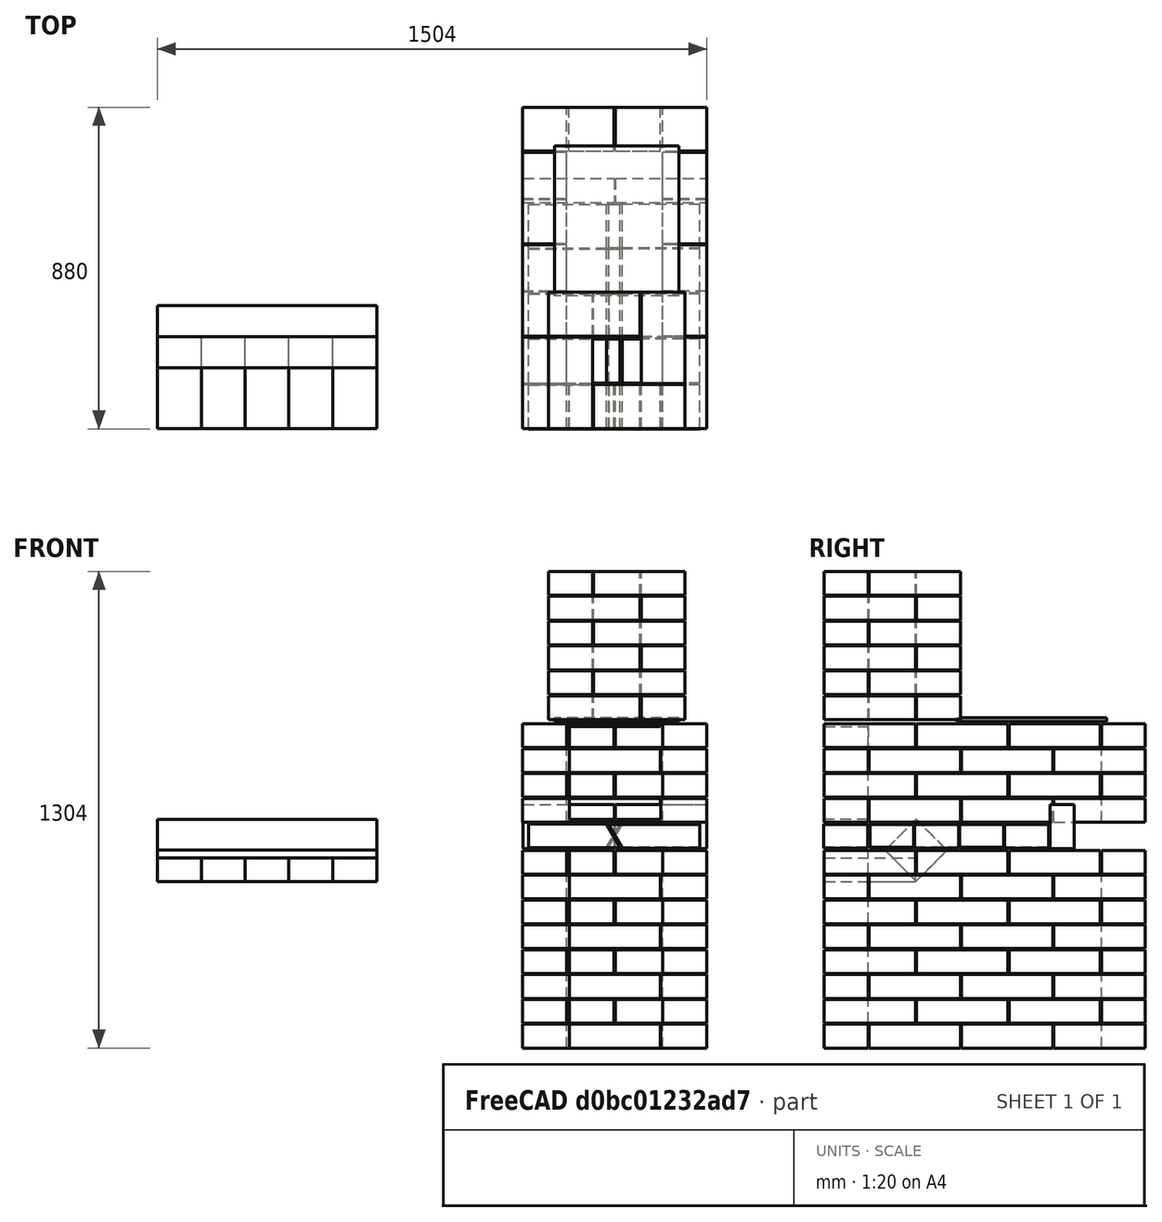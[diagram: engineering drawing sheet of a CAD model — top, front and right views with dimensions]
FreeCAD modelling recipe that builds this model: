
FCSTD DOCUMENT  (FreeCAD 0.19R24291 (Git))
Label: МиниАрийка
License: All rights reserved
LicenseURL: http://en.wikipedia.org/wiki/All_rights_reserved
objects: Part::Box×169, Part::Compound×30, Part::Cut×12, Part::Mirroring×2
note: 213 computed .brp shape members not serialized (recipe doc carries the construction recipe); baked Part::Feature solids carry a one-line shape summary decoded from their .brp

FEATURE [Part::Box] Box1  label="Куб1"
  AttacherType = Attacher::AttachEngine3D
  Height = 65
  Length = 250
  Width = 120
FEATURE [Part::Box] Box2  label="Куб2"
  AttacherType = Attacher::AttachEngine3D
  Height = 65
  Length = 250
  Placement = pos=(253,0,0) rot=(0,0,1;0rad)
  Width = 120
FEATURE [Part::Box] Box3  label="Куб3"
  AttacherType = Attacher::AttachEngine3D
  Height = 65
  Length = 250
  Placement = pos=(126.5,759,0) rot=(0,0,1;0rad)
  Width = 120
FEATURE [Part::Box] Box4  label="Куб4"
  AttacherType = Attacher::AttachEngine3D
  Height = 65
  Length = 250
  Placement = pos=(120,123,0) rot=(0,0,1;1.5708rad)
  Width = 120
FEATURE [Part::Box] Box5  label="Куб5"
  AttacherType = Attacher::AttachEngine3D
  Height = 65
  Length = 250
  Placement = pos=(120,376,0) rot=(0,0,1;1.5708rad)
  Width = 120
FEATURE [Part::Box] Box6  label="Куб6"
  AttacherType = Attacher::AttachEngine3D
  Height = 65
  Length = 250
  Placement = pos=(120,629,0) rot=(0,0,1;1.5708rad)
  Width = 120
FEATURE [Part::Box] Box7  label="Куб7"
  AttacherType = Attacher::AttachEngine3D
  Height = 65
  Length = 250
  Placement = pos=(503,123,0) rot=(0,0,1;1.5708rad)
  Width = 120
FEATURE [Part::Box] Box8  label="Куб8"
  AttacherType = Attacher::AttachEngine3D
  Height = 65
  Length = 250
  Placement = pos=(503,376,0) rot=(0,0,1;1.5708rad)
  Width = 120
FEATURE [Part::Box] Box9  label="Куб9"
  AttacherType = Attacher::AttachEngine3D
  Height = 65
  Length = 250
  Placement = pos=(503,629,0) rot=(0,0,1;1.5708rad)
  Width = 120
FEATURE [Part::Compound] Compound_row0
  Links = -> [Box1,Box2,Box3,Box4,Box5,Box6,Box7,Box8,Box9]
FEATURE [Part::Box] Box10  label="Куб10"
  AttacherType = Attacher::AttachEngine3D
  Height = 65
  Length = 250
  Placement = pos=(0,759,68) rot=(0,0,1;0rad)
  Width = 120
FEATURE [Part::Box] Box11  label="Куб11"
  AttacherType = Attacher::AttachEngine3D
  Height = 65
  Length = 250
  Placement = pos=(253,759,68) rot=(0,0,1;0rad)
  Width = 120
FEATURE [Part::Box] Box12  label="Куб12"
  AttacherType = Attacher::AttachEngine3D
  Height = 65
  Length = 250
  Placement = pos=(126.5,0,68) rot=(0,0,1;0rad)
  Width = 120
FEATURE [Part::Box] Box13  label="Куб13"
  AttacherType = Attacher::AttachEngine3D
  Height = 65
  Length = 250
  Placement = pos=(120,0,68) rot=(0,0,1;1.5708rad)
  Width = 120
FEATURE [Part::Box] Box14  label="Куб14"
  AttacherType = Attacher::AttachEngine3D
  Height = 65
  Length = 250
  Placement = pos=(120,253,68) rot=(0,0,1;1.5708rad)
  Width = 120
FEATURE [Part::Box] Box15  label="Куб15"
  AttacherType = Attacher::AttachEngine3D
  Height = 65
  Length = 250
  Placement = pos=(120,506,68) rot=(0,0,1;1.5708rad)
  Width = 120
FEATURE [Part::Box] Box16  label="Куб16"
  AttacherType = Attacher::AttachEngine3D
  Height = 65
  Length = 250
  Placement = pos=(503,0,68) rot=(0,0,1;1.5708rad)
  Width = 120
FEATURE [Part::Box] Box17  label="Куб17"
  AttacherType = Attacher::AttachEngine3D
  Height = 65
  Length = 250
  Placement = pos=(503,253,68) rot=(0,0,1;1.5708rad)
  Width = 120
FEATURE [Part::Box] Box18  label="Куб18"
  AttacherType = Attacher::AttachEngine3D
  Height = 65
  Length = 250
  Placement = pos=(503,506,68) rot=(0,0,1;1.5708rad)
  Width = 120
FEATURE [Part::Compound] Compound_row1
  Links = -> [Box10,Box11,Box12,Box13,Box14,Box15,Box16,Box17,Box18]
FEATURE [Part::Box] Box19  label="Куб19"
  AttacherType = Attacher::AttachEngine3D
  Height = 65
  Length = 250
  Placement = pos=(0,0,136) rot=(0,0,1;0rad)
  Width = 120
FEATURE [Part::Box] Box20  label="Куб20"
  AttacherType = Attacher::AttachEngine3D
  Height = 65
  Length = 250
  Placement = pos=(253,0,136) rot=(0,0,1;0rad)
  Width = 120
FEATURE [Part::Box] Box21  label="Куб21"
  AttacherType = Attacher::AttachEngine3D
  Height = 65
  Length = 250
  Placement = pos=(126.5,759,136) rot=(0,0,1;0rad)
  Width = 120
FEATURE [Part::Box] Box22  label="Куб22"
  AttacherType = Attacher::AttachEngine3D
  Height = 65
  Length = 250
  Placement = pos=(120,123,136) rot=(0,0,1;1.5708rad)
  Width = 120
FEATURE [Part::Box] Box23  label="Куб23"
  AttacherType = Attacher::AttachEngine3D
  Height = 65
  Length = 250
  Placement = pos=(120,376,136) rot=(0,0,1;1.5708rad)
  Width = 120
FEATURE [Part::Box] Box24  label="Куб24"
  AttacherType = Attacher::AttachEngine3D
  Height = 65
  Length = 250
  Placement = pos=(120,629,136) rot=(0,0,1;1.5708rad)
  Width = 120
FEATURE [Part::Box] Box25  label="Куб25"
  AttacherType = Attacher::AttachEngine3D
  Height = 65
  Length = 250
  Placement = pos=(503,123,136) rot=(0,0,1;1.5708rad)
  Width = 120
FEATURE [Part::Box] Box26  label="Куб26"
  AttacherType = Attacher::AttachEngine3D
  Height = 65
  Length = 250
  Placement = pos=(503,376,136) rot=(0,0,1;1.5708rad)
  Width = 120
FEATURE [Part::Box] Box27  label="Куб27"
  AttacherType = Attacher::AttachEngine3D
  Height = 65
  Length = 250
  Placement = pos=(503,629,136) rot=(0,0,1;1.5708rad)
  Width = 120
FEATURE [Part::Compound] Compound_row2
  Links = -> [Box19,Box20,Box21,Box22,Box23,Box24,Box25,Box26,Box27]
FEATURE [Part::Box] Box28  label="Куб28"
  AttacherType = Attacher::AttachEngine3D
  Height = 65
  Length = 250
  Placement = pos=(0,759,204) rot=(0,0,1;0rad)
  Width = 120
FEATURE [Part::Box] Box29  label="Куб29"
  AttacherType = Attacher::AttachEngine3D
  Height = 65
  Length = 250
  Placement = pos=(253,759,204) rot=(0,0,1;0rad)
  Width = 120
FEATURE [Part::Box] Box30  label="Куб30"
  AttacherType = Attacher::AttachEngine3D
  Height = 65
  Length = 250
  Placement = pos=(126.5,0,204) rot=(0,0,1;0rad)
  Width = 120
FEATURE [Part::Box] Box31  label="Куб31"
  AttacherType = Attacher::AttachEngine3D
  Height = 65
  Length = 250
  Placement = pos=(120,0,204) rot=(0,0,1;1.5708rad)
  Width = 120
FEATURE [Part::Box] Box32  label="Куб32"
  AttacherType = Attacher::AttachEngine3D
  Height = 65
  Length = 250
  Placement = pos=(120,253,204) rot=(0,0,1;1.5708rad)
  Width = 120
FEATURE [Part::Box] Box33  label="Куб33"
  AttacherType = Attacher::AttachEngine3D
  Height = 65
  Length = 250
  Placement = pos=(120,506,204) rot=(0,0,1;1.5708rad)
  Width = 120
FEATURE [Part::Box] Box34  label="Куб34"
  AttacherType = Attacher::AttachEngine3D
  Height = 65
  Length = 250
  Placement = pos=(503,0,204) rot=(0,0,1;1.5708rad)
  Width = 120
FEATURE [Part::Box] Box35  label="Куб35"
  AttacherType = Attacher::AttachEngine3D
  Height = 65
  Length = 250
  Placement = pos=(503,253,204) rot=(0,0,1;1.5708rad)
  Width = 120
FEATURE [Part::Box] Box36  label="Куб36"
  AttacherType = Attacher::AttachEngine3D
  Height = 65
  Length = 250
  Placement = pos=(503,506,204) rot=(0,0,1;1.5708rad)
  Width = 120
FEATURE [Part::Compound] Compound_row3
  Links = -> [Box28,Box29,Box30,Box31,Box32,Box33,Box34,Box35,Box36]
FEATURE [Part::Box] Box37  label="Куб37"
  AttacherType = Attacher::AttachEngine3D
  Height = 65
  Length = 250
  Placement = pos=(0,0,272) rot=(0,0,1;0rad)
  Width = 120
FEATURE [Part::Box] Box38  label="Куб38"
  AttacherType = Attacher::AttachEngine3D
  Height = 65
  Length = 250
  Placement = pos=(253,0,272) rot=(0,0,1;0rad)
  Width = 120
FEATURE [Part::Box] Box39  label="Куб39"
  AttacherType = Attacher::AttachEngine3D
  Height = 65
  Length = 250
  Placement = pos=(126.5,759,272) rot=(0,0,1;0rad)
  Width = 120
FEATURE [Part::Box] Box40  label="Куб40"
  AttacherType = Attacher::AttachEngine3D
  Height = 65
  Length = 250
  Placement = pos=(120,123,272) rot=(0,0,1;1.5708rad)
  Width = 120
FEATURE [Part::Box] Box41  label="Куб41"
  AttacherType = Attacher::AttachEngine3D
  Height = 65
  Length = 250
  Placement = pos=(120,376,272) rot=(0,0,1;1.5708rad)
  Width = 120
FEATURE [Part::Box] Box42  label="Куб42"
  AttacherType = Attacher::AttachEngine3D
  Height = 65
  Length = 250
  Placement = pos=(120,629,272) rot=(0,0,1;1.5708rad)
  Width = 120
FEATURE [Part::Box] Box43  label="Куб43"
  AttacherType = Attacher::AttachEngine3D
  Height = 65
  Length = 250
  Placement = pos=(503,123,272) rot=(0,0,1;1.5708rad)
  Width = 120
FEATURE [Part::Box] Box44  label="Куб44"
  AttacherType = Attacher::AttachEngine3D
  Height = 65
  Length = 250
  Placement = pos=(503,376,272) rot=(0,0,1;1.5708rad)
  Width = 120
FEATURE [Part::Box] Box45  label="Куб45"
  AttacherType = Attacher::AttachEngine3D
  Height = 65
  Length = 250
  Placement = pos=(503,629,272) rot=(0,0,1;1.5708rad)
  Width = 120
FEATURE [Part::Compound] Compound_row4
  Links = -> [Box37,Box38,Box39,Box40,Box41,Box42,Box43,Box44,Box45]
FEATURE [Part::Box] Box46  label="Куб46"
  AttacherType = Attacher::AttachEngine3D
  Height = 65
  Length = 250
  Placement = pos=(0,759,340) rot=(0,0,1;0rad)
  Width = 120
FEATURE [Part::Box] Box47  label="Куб47"
  AttacherType = Attacher::AttachEngine3D
  Height = 65
  Length = 250
  Placement = pos=(253,759,340) rot=(0,0,1;0rad)
  Width = 120
FEATURE [Part::Box] Box48  label="Куб48"
  AttacherType = Attacher::AttachEngine3D
  Height = 65
  Length = 250
  Placement = pos=(126.5,0,340) rot=(0,0,1;0rad)
  Width = 120
FEATURE [Part::Box] Box49  label="Куб49"
  AttacherType = Attacher::AttachEngine3D
  Height = 65
  Length = 250
  Placement = pos=(120,0,340) rot=(0,0,1;1.5708rad)
  Width = 120
FEATURE [Part::Box] Box50  label="Куб50"
  AttacherType = Attacher::AttachEngine3D
  Height = 65
  Length = 250
  Placement = pos=(120,253,340) rot=(0,0,1;1.5708rad)
  Width = 120
FEATURE [Part::Box] Box51  label="Куб51"
  AttacherType = Attacher::AttachEngine3D
  Height = 65
  Length = 250
  Placement = pos=(120,506,340) rot=(0,0,1;1.5708rad)
  Width = 120
FEATURE [Part::Box] Box52  label="Куб52"
  AttacherType = Attacher::AttachEngine3D
  Height = 65
  Length = 250
  Placement = pos=(503,0,340) rot=(0,0,1;1.5708rad)
  Width = 120
FEATURE [Part::Box] Box53  label="Куб53"
  AttacherType = Attacher::AttachEngine3D
  Height = 65
  Length = 250
  Placement = pos=(503,253,340) rot=(0,0,1;1.5708rad)
  Width = 120
FEATURE [Part::Box] Box54  label="Куб54"
  AttacherType = Attacher::AttachEngine3D
  Height = 65
  Length = 250
  Placement = pos=(503,506,340) rot=(0,0,1;1.5708rad)
  Width = 120
FEATURE [Part::Compound] Compound_row5
  Links = -> [Box46,Box47,Box48,Box49,Box50,Box51,Box52,Box53,Box54]
FEATURE [Part::Box] Box55  label="Куб55"
  AttacherType = Attacher::AttachEngine3D
  Height = 65
  Length = 250
  Placement = pos=(0,0,408) rot=(0,0,1;0rad)
  Width = 120
FEATURE [Part::Box] Box56  label="Куб56"
  AttacherType = Attacher::AttachEngine3D
  Height = 65
  Length = 250
  Placement = pos=(253,0,408) rot=(0,0,1;0rad)
  Width = 120
FEATURE [Part::Box] Box57  label="Куб57"
  AttacherType = Attacher::AttachEngine3D
  Height = 65
  Length = 250
  Placement = pos=(126.5,759,408) rot=(0,0,1;0rad)
  Width = 120
FEATURE [Part::Box] Box58  label="Куб58"
  AttacherType = Attacher::AttachEngine3D
  Height = 65
  Length = 250
  Placement = pos=(120,123,408) rot=(0,0,1;1.5708rad)
  Width = 120
FEATURE [Part::Box] Box59  label="Куб59"
  AttacherType = Attacher::AttachEngine3D
  Height = 65
  Length = 250
  Placement = pos=(120,376,408) rot=(0,0,1;1.5708rad)
  Width = 120
FEATURE [Part::Box] Box60  label="Куб60"
  AttacherType = Attacher::AttachEngine3D
  Height = 65
  Length = 250
  Placement = pos=(120,629,408) rot=(0,0,1;1.5708rad)
  Width = 120
FEATURE [Part::Box] Box61  label="Куб61"
  AttacherType = Attacher::AttachEngine3D
  Height = 65
  Length = 250
  Placement = pos=(503,123,408) rot=(0,0,1;1.5708rad)
  Width = 120
FEATURE [Part::Box] Box62  label="Куб62"
  AttacherType = Attacher::AttachEngine3D
  Height = 65
  Length = 250
  Placement = pos=(503,376,408) rot=(0,0,1;1.5708rad)
  Width = 120
FEATURE [Part::Box] Box63  label="Куб63"
  AttacherType = Attacher::AttachEngine3D
  Height = 65
  Length = 250
  Placement = pos=(503,629,408) rot=(0,0,1;1.5708rad)
  Width = 120
FEATURE [Part::Compound] Compound_row6
  Links = -> [Box55,Box56,Box57,Box58,Box59,Box60,Box61,Box62,Box63]
FEATURE [Part::Box] Box64  label="Куб64"
  AttacherType = Attacher::AttachEngine3D
  Height = 65
  Length = 250
  Placement = pos=(0,759,476) rot=(0,0,1;0rad)
  Width = 120
FEATURE [Part::Box] Box65  label="Куб65"
  AttacherType = Attacher::AttachEngine3D
  Height = 65
  Length = 250
  Placement = pos=(253,759,476) rot=(0,0,1;0rad)
  Width = 120
FEATURE [Part::Box] Box66  label="Куб66"
  AttacherType = Attacher::AttachEngine3D
  Height = 65
  Length = 250
  Placement = pos=(126.5,0,476) rot=(0,0,1;0rad)
  Width = 120
FEATURE [Part::Box] Box67  label="Куб67"
  AttacherType = Attacher::AttachEngine3D
  Height = 65
  Length = 250
  Placement = pos=(120,0,476) rot=(0,0,1;1.5708rad)
  Width = 120
FEATURE [Part::Box] Box68  label="Куб68"
  AttacherType = Attacher::AttachEngine3D
  Height = 65
  Length = 250
  Placement = pos=(120,253,476) rot=(0,0,1;1.5708rad)
  Width = 120
FEATURE [Part::Box] Box69  label="Куб69"
  AttacherType = Attacher::AttachEngine3D
  Height = 65
  Length = 250
  Placement = pos=(120,506,476) rot=(0,0,1;1.5708rad)
  Width = 120
FEATURE [Part::Box] Box70  label="Куб70"
  AttacherType = Attacher::AttachEngine3D
  Height = 65
  Length = 250
  Placement = pos=(503,0,476) rot=(0,0,1;1.5708rad)
  Width = 120
FEATURE [Part::Box] Box71  label="Куб71"
  AttacherType = Attacher::AttachEngine3D
  Height = 65
  Length = 250
  Placement = pos=(503,253,476) rot=(0,0,1;1.5708rad)
  Width = 120
FEATURE [Part::Box] Box72  label="Куб72"
  AttacherType = Attacher::AttachEngine3D
  Height = 65
  Length = 250
  Placement = pos=(503,506,476) rot=(0,0,1;1.5708rad)
  Width = 120
FEATURE [Part::Compound] Compound_row7
  Links = -> [Box64,Box65,Box66,Box67,Box68,Box69,Box70,Box71,Box72]
FEATURE [Part::Box] Box090  label="Куб024"
  AttacherType = Attacher::AttachEngine3D
  Height = 65
  Length = 250
  Placement = pos=(120,0,455) rot=(0,0,1;1.5708rad)
  Width = 120
FEATURE [Part::Box] Box103  label="Куб029"
  AttacherType = Attacher::AttachEngine3D
  Height = 65
  Length = 250
  Placement = pos=(240,0,455) rot=(0,0,1;1.5708rad)
  Width = 120
FEATURE [Part::Box] Box104  label="Куб030"
  AttacherType = Attacher::AttachEngine3D
  Height = 65
  Length = 250
  Placement = pos=(360,0,455) rot=(0,0,1;1.5708rad)
  Width = 120
FEATURE [Part::Box] Box105  label="Куб031"
  AttacherType = Attacher::AttachEngine3D
  Height = 65
  Length = 250
  Placement = pos=(480,0,455) rot=(0,0,1;1.5708rad)
  Width = 120
FEATURE [Part::Box] Box106  label="Куб032"
  AttacherType = Attacher::AttachEngine3D
  Height = 65
  Length = 250
  Placement = pos=(600,0,455) rot=(0,0,1;1.5708rad)
  Width = 120
FEATURE [Part::Box] Box134  label="Куб049"
  AttacherType = Attacher::AttachEngine3D
  Height = 65
  Length = 250
  Placement = pos=(360,0,455) rot=(0,0,1;1.5708rad)
  Width = 120
FEATURE [Part::Box] Box135  label="Куб050"
  AttacherType = Attacher::AttachEngine3D
  Height = 65
  Length = 250
  Placement = pos=(480,0,455) rot=(0,0,1;1.5708rad)
  Width = 120
FEATURE [Part::Box] Box136  label="Куб051"
  AttacherType = Attacher::AttachEngine3D
  Height = 65
  Length = 250
  Placement = pos=(240,0,455) rot=(0,0,1;1.5708rad)
  Width = 120
FEATURE [Part::Box] Box137  label="Куб052"
  AttacherType = Attacher::AttachEngine3D
  Height = 65
  Length = 250
  Placement = pos=(600,0,455) rot=(0,0,1;1.5708rad)
  Width = 120
FEATURE [Part::Box] Box138  label="Куб053"
  AttacherType = Attacher::AttachEngine3D
  Height = 65
  Length = 250
  Placement = pos=(120,0,455) rot=(0,0,1;1.5708rad)
  Width = 120
FEATURE [Part::Compound] Compound039
  Links = -> [Box138,Box136,Box134,Box135,Box137]
  Placement = pos=(-1000,0,0) rot=(0,0,1;0rad)
FEATURE [Part::Box] Box139  label="Куб054"
  AttacherType = Attacher::AttachEngine3D
  Height = 120
  Length = 600
  Placement = pos=(-1000,251.73,456.377) rot=(1,0,0;0.785398rad)
  Width = 120
FEATURE [Part::Box] Box140  label="Куб055"
  AttacherType = Attacher::AttachEngine3D
  Height = 65
  Length = 250
  Placement = pos=(500,678,549) rot=(1,0,0;1.5708rad)
  Width = 120
FEATURE [Part::Box] Box141  label="Куб056"
  AttacherType = Attacher::AttachEngine3D
  Height = 65
  Length = 250
  Placement = pos=(753,678,549) rot=(1,0,0;1.5708rad)
  Width = 120
FEATURE [Part::Compound] Compound
  Links = -> [Box141,Box140]
  Placement = pos=(-499,6,-3) rot=(0,0,1;0rad)
FEATURE [Part::Box] Box  label="Топка"
  AttacherType = Attacher::AttachEngine3D
  Height = 545
  Length = 250
  Placement = pos=(128,-38,0) rot=(0,0,1;0rad)
  Width = 250
FEATURE [Part::Compound] Compound040
  Links = -> [Compound_row0,Compound_row1,Compound_row2,Compound_row3,Compound_row4,Compound_row5,Compound_row6,Compound_row7]
FEATURE [Part::Cut] Cut
  Base = -> Compound040
  Tool = -> Box
FEATURE [Part::Box] Box001  label="Куб001"
  AttacherType = Attacher::AttachEngine3D
  Height = 65
  Length = 250
  Placement = pos=(187.928,0,108.5) rot=(0,1,0;1.0472rad)
  Width = 120
FEATURE [Part::Box] Box142  label="Куб"
  AttacherType = Attacher::AttachEngine3D
  Height = 65
  Length = 250
  Width = 120
FEATURE [Part::Box] Box006  label="Куб006"
  AttacherType = Attacher::AttachEngine3D
  Height = 65
  Length = 250
  Placement = pos=(187.928,0,108.5) rot=(0,1,0;1.0472rad)
  Width = 120
FEATURE [Part::Box] Box007  label="Куб007"
  AttacherType = Attacher::AttachEngine3D
  Height = 65
  Length = 250
  Width = 120
FEATURE [Part::Cut] Cut003
  Base = -> Box007
  Placement = pos=(469,0,64) rot=(0,1,0;3.14159rad)
  Tool = -> Box006
FEATURE [Part::Box] Box005  label="Куб005"
  AttacherType = Attacher::AttachEngine3D
  Height = 65
  Length = 250
  Width = 120
FEATURE [Part::Box] Box008  label="Куб008"
  AttacherType = Attacher::AttachEngine3D
  Height = 65
  Length = 250
  Placement = pos=(187.928,0,108.5) rot=(0,1,0;1.0472rad)
  Width = 120
FEATURE [Part::Box] Box009  label="Куб009"
  AttacherType = Attacher::AttachEngine3D
  Height = 65
  Length = 250
  Width = 120
FEATURE [Part::Cut] Cut004
  Base = -> Box142
  Tool = -> Box001
FEATURE [Part::Box] Box002  label="Куб002"
  AttacherType = Attacher::AttachEngine3D
  Height = 65
  Length = 250
  Placement = pos=(187.928,0,108.5) rot=(0,1,0;1.0472rad)
  Width = 120
FEATURE [Part::Box] Box004  label="Куб004"
  AttacherType = Attacher::AttachEngine3D
  Height = 65
  Length = 250
  Placement = pos=(187.928,0,108.5) rot=(0,1,0;1.0472rad)
  Width = 120
FEATURE [Part::Cut] Cut002
  Base = -> Box005
  Tool = -> Box004
FEATURE [Part::Compound] Compound001
  Links = -> [Cut003,Cut002]
  Placement = pos=(0,123,0) rot=(0,0,1;0rad)
FEATURE [Part::Box] Box003  label="Куб003"
  AttacherType = Attacher::AttachEngine3D
  Height = 65
  Length = 250
  Width = 120
FEATURE [Part::Cut] Cut001
  Base = -> Box003
  Placement = pos=(469,0,64) rot=(0,1,0;3.14159rad)
  Tool = -> Box002
FEATURE [Part::Compound] Compound041
  Links = -> [Cut001,Cut004]
FEATURE [Part::Mirroring] Part__Mirroring  label="Compound (Mirror #1)"
  Base = (234.5,60,0)
  Normal = (0,0,1)
  Placement = pos=(0,0,65) rot=(0,0,1;0rad)
  Source = -> Compound041
FEATURE [Part::Box] Box012  label="Куб012"
  AttacherType = Attacher::AttachEngine3D
  Height = 65
  Length = 250
  Placement = pos=(187.928,0,108.5) rot=(0,1,0;1.0472rad)
  Width = 120
FEATURE [Part::Box] Box013  label="Куб013"
  AttacherType = Attacher::AttachEngine3D
  Height = 65
  Length = 250
  Width = 120
FEATURE [Part::Box] Box010  label="Куб010"
  AttacherType = Attacher::AttachEngine3D
  Height = 65
  Length = 250
  Width = 120
FEATURE [Part::Box] Box011  label="Куб011"
  AttacherType = Attacher::AttachEngine3D
  Height = 65
  Length = 250
  Placement = pos=(187.928,0,108.5) rot=(0,1,0;1.0472rad)
  Width = 120
FEATURE [Part::Cut] Cut005
  Base = -> Box010
  Tool = -> Box011
FEATURE [Part::Cut] Cut006
  Base = -> Box009
  Placement = pos=(469,0,64) rot=(0,1,0;3.14159rad)
  Tool = -> Box008
FEATURE [Part::Compound] Compound002
  Links = -> [Cut006,Cut005]
  Placement = pos=(0,246,0) rot=(0,0,1;0rad)
FEATURE [Part::Mirroring] Part__Mirroring001  label="Compound002 (Mirror #2)"
  Base = (0,0,0)
  Normal = (0,0,1)
  Placement = pos=(0,0,66) rot=(0,0,1;0rad)
  Source = -> Compound002
FEATURE [Part::Box] Box014  label="Куб014"
  AttacherType = Attacher::AttachEngine3D
  Height = 65
  Length = 250
  Width = 120
FEATURE [Part::Box] Box015  label="Куб015"
  AttacherType = Attacher::AttachEngine3D
  Height = 65
  Length = 250
  Placement = pos=(187.928,0,108.5) rot=(0,1,0;1.0472rad)
  Width = 120
FEATURE [Part::Cut] Cut007
  Base = -> Box014
  Tool = -> Box015
FEATURE [Part::Cut] Cut008
  Base = -> Box013
  Placement = pos=(469,0,64) rot=(0,1,0;3.14159rad)
  Tool = -> Box012
FEATURE [Part::Compound] Compound003
  Links = -> [Cut008,Cut007]
  Placement = pos=(0,369,0) rot=(0,0,1;0rad)
FEATURE [Part::Box] Box016  label="Куб016"
  AttacherType = Attacher::AttachEngine3D
  Height = 65
  Length = 250
  Placement = pos=(187.928,0,108.5) rot=(0,1,0;1.0472rad)
  Width = 120
FEATURE [Part::Box] Box017  label="Куб017"
  AttacherType = Attacher::AttachEngine3D
  Height = 65
  Length = 250
  Width = 120
FEATURE [Part::Cut] Cut009
  Base = -> Box017
  Placement = pos=(469,0,64) rot=(0,1,0;3.14159rad)
  Tool = -> Box016
FEATURE [Part::Box] Box018  label="Куб018"
  AttacherType = Attacher::AttachEngine3D
  Height = 65
  Length = 250
  Width = 120
FEATURE [Part::Box] Box019  label="Куб019"
  AttacherType = Attacher::AttachEngine3D
  Height = 65
  Length = 250
  Placement = pos=(187.928,0,108.5) rot=(0,1,0;1.0472rad)
  Width = 120
FEATURE [Part::Cut] Cut010
  Base = -> Box018
  Tool = -> Box019
FEATURE [Part::Compound] Compound004
  Links = -> [Cut009,Cut010]
  Placement = pos=(0,-126,0) rot=(0,0,1;0rad)
FEATURE [Part::Compound] Compound005
  Links = -> [Compound001,Compound003,Part__Mirroring,Part__Mirroring001,Compound004,Compound041,Compound002]
  Placement = pos=(16,125,548) rot=(0,0,1;0rad)
FEATURE [Part::Box] Box1043  label="Куб057"
  AttacherType = Attacher::AttachEngine3D
  Height = 65
  Length = 250
  Width = 120
FEATURE [Part::Box] Box2010  label="Куб058"
  AttacherType = Attacher::AttachEngine3D
  Height = 65
  Length = 250
  Placement = pos=(253,0,0) rot=(0,0,1;0rad)
  Width = 120
FEATURE [Part::Box] Box3010  label="Куб059"
  AttacherType = Attacher::AttachEngine3D
  Height = 65
  Length = 250
  Placement = pos=(126.5,759,0) rot=(0,0,1;0rad)
  Width = 120
FEATURE [Part::Box] Box4010  label="Куб060"
  AttacherType = Attacher::AttachEngine3D
  Height = 65
  Length = 250
  Placement = pos=(120,123,0) rot=(0,0,1;1.5708rad)
  Width = 120
FEATURE [Part::Box] Box5010  label="Куб061"
  AttacherType = Attacher::AttachEngine3D
  Height = 65
  Length = 250
  Placement = pos=(120,376,0) rot=(0,0,1;1.5708rad)
  Width = 120
FEATURE [Part::Box] Box6010  label="Куб062"
  AttacherType = Attacher::AttachEngine3D
  Height = 65
  Length = 250
  Placement = pos=(120,629,0) rot=(0,0,1;1.5708rad)
  Width = 120
FEATURE [Part::Box] Box7003  label="Куб063"
  AttacherType = Attacher::AttachEngine3D
  Height = 65
  Length = 250
  Placement = pos=(503,123,0) rot=(0,0,1;1.5708rad)
  Width = 120
FEATURE [Part::Box] Box8001  label="Куб064"
  AttacherType = Attacher::AttachEngine3D
  Height = 65
  Length = 250
  Placement = pos=(503,376,0) rot=(0,0,1;1.5708rad)
  Width = 120
FEATURE [Part::Box] Box9001  label="Куб065"
  AttacherType = Attacher::AttachEngine3D
  Height = 65
  Length = 250
  Placement = pos=(503,629,0) rot=(0,0,1;1.5708rad)
  Width = 120
FEATURE [Part::Compound] Compound_row0001
  Links = -> [Box1043,Box2010,Box3010,Box4010,Box5010,Box6010,Box7003,Box8001,Box9001]
FEATURE [Part::Box] Box10044  label="Куб066"
  AttacherType = Attacher::AttachEngine3D
  Height = 65
  Length = 250
  Placement = pos=(0,759,68) rot=(0,0,1;0rad)
  Width = 120
FEATURE [Part::Box] Box11001  label="Куб067"
  AttacherType = Attacher::AttachEngine3D
  Height = 65
  Length = 250
  Placement = pos=(253,759,68) rot=(0,0,1;0rad)
  Width = 120
FEATURE [Part::Box] Box12001  label="Куб068"
  AttacherType = Attacher::AttachEngine3D
  Height = 65
  Length = 250
  Placement = pos=(126.5,0,68) rot=(0,0,1;0rad)
  Width = 120
FEATURE [Part::Box] Box13010  label="Куб069"
  AttacherType = Attacher::AttachEngine3D
  Height = 65
  Length = 250
  Placement = pos=(120,0,68) rot=(0,0,1;1.5708rad)
  Width = 120
FEATURE [Part::Box] Box14003  label="Куб070"
  AttacherType = Attacher::AttachEngine3D
  Height = 65
  Length = 250
  Placement = pos=(120,253,68) rot=(0,0,1;1.5708rad)
  Width = 120
FEATURE [Part::Box] Box15001  label="Куб071"
  AttacherType = Attacher::AttachEngine3D
  Height = 65
  Length = 250
  Placement = pos=(120,506,68) rot=(0,0,1;1.5708rad)
  Width = 120
FEATURE [Part::Box] Box16001  label="Куб072"
  AttacherType = Attacher::AttachEngine3D
  Height = 65
  Length = 250
  Placement = pos=(503,0,68) rot=(0,0,1;1.5708rad)
  Width = 120
FEATURE [Part::Box] Box17001  label="Куб073"
  AttacherType = Attacher::AttachEngine3D
  Height = 65
  Length = 250
  Placement = pos=(503,253,68) rot=(0,0,1;1.5708rad)
  Width = 120
FEATURE [Part::Box] Box18001  label="Куб074"
  AttacherType = Attacher::AttachEngine3D
  Height = 65
  Length = 250
  Placement = pos=(503,506,68) rot=(0,0,1;1.5708rad)
  Width = 120
FEATURE [Part::Compound] Compound_row1001
  Links = -> [Box10044,Box11001,Box12001,Box13010,Box14003,Box15001,Box16001,Box17001,Box18001]
FEATURE [Part::Box] Box19001  label="Куб075"
  AttacherType = Attacher::AttachEngine3D
  Height = 65
  Length = 250
  Placement = pos=(0,0,136) rot=(0,0,1;0rad)
  Width = 120
FEATURE [Part::Box] Box20011  label="Куб076"
  AttacherType = Attacher::AttachEngine3D
  Height = 65
  Length = 250
  Placement = pos=(253,0,136) rot=(0,0,1;0rad)
  Width = 120
FEATURE [Part::Box] Box21001  label="Куб077"
  AttacherType = Attacher::AttachEngine3D
  Height = 65
  Length = 250
  Placement = pos=(126.5,759,136) rot=(0,0,1;0rad)
  Width = 120
FEATURE [Part::Box] Box22001  label="Куб078"
  AttacherType = Attacher::AttachEngine3D
  Height = 65
  Length = 250
  Placement = pos=(120,123,136) rot=(0,0,1;1.5708rad)
  Width = 120
FEATURE [Part::Box] Box23001  label="Куб079"
  AttacherType = Attacher::AttachEngine3D
  Height = 65
  Length = 250
  Placement = pos=(120,376,136) rot=(0,0,1;1.5708rad)
  Width = 120
FEATURE [Part::Box] Box24001  label="Куб080"
  AttacherType = Attacher::AttachEngine3D
  Height = 65
  Length = 250
  Placement = pos=(120,629,136) rot=(0,0,1;1.5708rad)
  Width = 120
FEATURE [Part::Box] Box25001  label="Куб081"
  AttacherType = Attacher::AttachEngine3D
  Height = 65
  Length = 250
  Placement = pos=(503,123,136) rot=(0,0,1;1.5708rad)
  Width = 120
FEATURE [Part::Box] Box26001  label="Куб082"
  AttacherType = Attacher::AttachEngine3D
  Height = 65
  Length = 250
  Placement = pos=(503,376,136) rot=(0,0,1;1.5708rad)
  Width = 120
FEATURE [Part::Box] Box27001  label="Куб083"
  AttacherType = Attacher::AttachEngine3D
  Height = 65
  Length = 250
  Placement = pos=(503,629,136) rot=(0,0,1;1.5708rad)
  Width = 120
FEATURE [Part::Compound] Compound_row2001
  Links = -> [Box19001,Box20011,Box21001,Box22001,Box23001,Box24001,Box25001,Box26001,Box27001]
FEATURE [Part::Box] Box28001  label="Куб084"
  AttacherType = Attacher::AttachEngine3D
  Height = 65
  Length = 250
  Placement = pos=(0,759,204) rot=(0,0,1;0rad)
  Width = 120
FEATURE [Part::Box] Box29001  label="Куб085"
  AttacherType = Attacher::AttachEngine3D
  Height = 65
  Length = 250
  Placement = pos=(253,759,204) rot=(0,0,1;0rad)
  Width = 120
FEATURE [Part::Box] Box30011  label="Куб086"
  AttacherType = Attacher::AttachEngine3D
  Height = 65
  Length = 250
  Placement = pos=(126.5,0,204) rot=(0,0,1;0rad)
  Width = 120
FEATURE [Part::Box] Box31001  label="Куб087"
  AttacherType = Attacher::AttachEngine3D
  Height = 65
  Length = 250
  Placement = pos=(120,0,204) rot=(0,0,1;1.5708rad)
  Width = 120
FEATURE [Part::Box] Box32001  label="Куб088"
  AttacherType = Attacher::AttachEngine3D
  Height = 65
  Length = 250
  Placement = pos=(120,253,204) rot=(0,0,1;1.5708rad)
  Width = 120
FEATURE [Part::Box] Box33001  label="Куб089"
  AttacherType = Attacher::AttachEngine3D
  Height = 65
  Length = 250
  Placement = pos=(120,506,204) rot=(0,0,1;1.5708rad)
  Width = 120
FEATURE [Part::Box] Box34001  label="Куб090"
  AttacherType = Attacher::AttachEngine3D
  Height = 65
  Length = 250
  Placement = pos=(503,0,204) rot=(0,0,1;1.5708rad)
  Width = 120
FEATURE [Part::Box] Box35001  label="Куб091"
  AttacherType = Attacher::AttachEngine3D
  Height = 65
  Length = 250
  Placement = pos=(503,253,204) rot=(0,0,1;1.5708rad)
  Width = 120
FEATURE [Part::Box] Box36001  label="Куб092"
  AttacherType = Attacher::AttachEngine3D
  Height = 65
  Length = 250
  Placement = pos=(503,506,204) rot=(0,0,1;1.5708rad)
  Width = 120
FEATURE [Part::Compound] Compound_row3001
  Links = -> [Box28001,Box29001,Box30011,Box31001,Box32001,Box33001,Box34001,Box35001,Box36001]
FEATURE [Part::Compound] Compound042
  Links = -> [Compound_row0001,Compound_row1001,Compound_row2001,Compound_row3001]
  Placement = pos=(0,0,618) rot=(0,0,1;0rad)
FEATURE [Part::Box] Box36002  label="Куб093"
  AttacherType = Attacher::AttachEngine3D
  Height = 65
  Length = 250
  Placement = pos=(123,253,0) rot=(0,0,1;0rad)
  Width = 120
FEATURE [Part::Box] Box36003  label="Куб094"
  AttacherType = Attacher::AttachEngine3D
  Height = 65
  Length = 250
  Placement = pos=(0,253,340) rot=(0,0,1;0rad)
  Width = 120
FEATURE [Part::Box] Box36004  label="Куб095"
  AttacherType = Attacher::AttachEngine3D
  Height = 65
  Length = 250
  Placement = pos=(123,0,340) rot=(0,0,1;0rad)
  Width = 120
FEATURE [Part::Box] Box36005  label="Куб096"
  AttacherType = Attacher::AttachEngine3D
  Height = 65
  Length = 250
  Placement = pos=(120,0,340) rot=(0,0,1;1.5708rad)
  Width = 120
FEATURE [Part::Box] Box36006  label="Куб097"
  AttacherType = Attacher::AttachEngine3D
  Height = 65
  Length = 250
  Placement = pos=(373,123,340) rot=(0,0,1;1.5708rad)
  Width = 120
FEATURE [Part::Compound] Compound_row3003
  Links = -> [Box36003,Box36004,Box36005,Box36006]
FEATURE [Part::Box] Box36007  label="Куб098"
  AttacherType = Attacher::AttachEngine3D
  Height = 65
  Length = 250
  Placement = pos=(0,0,272) rot=(0,0,1;0rad)
  Width = 120
FEATURE [Part::Box] Box36008  label="Куб099"
  AttacherType = Attacher::AttachEngine3D
  Height = 65
  Length = 250
  Placement = pos=(123,253,272) rot=(0,0,1;0rad)
  Width = 120
FEATURE [Part::Box] Box36009  label="Куб100"
  AttacherType = Attacher::AttachEngine3D
  Height = 65
  Length = 250
  Placement = pos=(120,123,272) rot=(0,0,1;1.5708rad)
  Width = 120
FEATURE [Part::Box] Box36010  label="Куб101"
  AttacherType = Attacher::AttachEngine3D
  Height = 65
  Length = 250
  Placement = pos=(373,0,272) rot=(0,0,1;1.5708rad)
  Width = 120
FEATURE [Part::Compound] Compound_row3002
  Links = -> [Box36007,Box36008,Box36009,Box36010]
FEATURE [Part::Box] Box36011  label="Куб102"
  AttacherType = Attacher::AttachEngine3D
  Height = 65
  Length = 250
  Placement = pos=(373,0,0) rot=(0,0,1;1.5708rad)
  Width = 120
FEATURE [Part::Box] Box36012  label="Куб103"
  AttacherType = Attacher::AttachEngine3D
  Height = 65
  Length = 250
  Placement = pos=(373,123,68) rot=(0,0,1;1.5708rad)
  Width = 120
FEATURE [Part::Box] Box36013  label="Куб104"
  AttacherType = Attacher::AttachEngine3D
  Height = 65
  Length = 250
  Placement = pos=(0,0,136) rot=(0,0,1;0rad)
  Width = 120
FEATURE [Part::Box] Box36014  label="Куб105"
  AttacherType = Attacher::AttachEngine3D
  Height = 65
  Length = 250
  Placement = pos=(123,253,136) rot=(0,0,1;0rad)
  Width = 120
FEATURE [Part::Box] Box36015  label="Куб106"
  AttacherType = Attacher::AttachEngine3D
  Height = 65
  Length = 250
  Placement = pos=(120,123,136) rot=(0,0,1;1.5708rad)
  Width = 120
FEATURE [Part::Box] Box36016  label="Куб107"
  AttacherType = Attacher::AttachEngine3D
  Height = 65
  Length = 250
  Placement = pos=(373,0,136) rot=(0,0,1;1.5708rad)
  Width = 120
FEATURE [Part::Compound] Compound_row3005
  Links = -> [Box36013,Box36014,Box36015,Box36016]
FEATURE [Part::Box] Box36017  label="Куб108"
  AttacherType = Attacher::AttachEngine3D
  Height = 65
  Length = 250
  Placement = pos=(120,123,0) rot=(0,0,1;1.5708rad)
  Width = 120
FEATURE [Part::Box] Box36018  label="Куб109"
  AttacherType = Attacher::AttachEngine3D
  Height = 65
  Length = 250
  Placement = pos=(0,253,68) rot=(0,0,1;0rad)
  Width = 120
FEATURE [Part::Box] Box36019  label="Куб110"
  AttacherType = Attacher::AttachEngine3D
  Height = 65
  Length = 250
  Placement = pos=(123,0,68) rot=(0,0,1;0rad)
  Width = 120
FEATURE [Part::Box] Box36020  label="Куб111"
  AttacherType = Attacher::AttachEngine3D
  Height = 65
  Length = 250
  Placement = pos=(120,0,68) rot=(0,0,1;1.5708rad)
  Width = 120
FEATURE [Part::Box] Box36021  label="Куб112"
  AttacherType = Attacher::AttachEngine3D
  Height = 65
  Length = 250
  Placement = pos=(0,253,204) rot=(0,0,1;0rad)
  Width = 120
FEATURE [Part::Box] Box36022  label="Куб113"
  AttacherType = Attacher::AttachEngine3D
  Height = 65
  Length = 250
  Placement = pos=(123,0,204) rot=(0,0,1;0rad)
  Width = 120
FEATURE [Part::Box] Box36023  label="Куб114"
  AttacherType = Attacher::AttachEngine3D
  Height = 65
  Length = 250
  Placement = pos=(120,0,204) rot=(0,0,1;1.5708rad)
  Width = 120
FEATURE [Part::Box] Box36024  label="Куб115"
  AttacherType = Attacher::AttachEngine3D
  Height = 65
  Length = 250
  Placement = pos=(373,123,204) rot=(0,0,1;1.5708rad)
  Width = 120
FEATURE [Part::Compound] Compound_row3006
  Links = -> [Box36021,Box36022,Box36023,Box36024]
FEATURE [Part::Compound] Compound_row3007
  Links = -> [Box36018,Box36019,Box36020,Box36012]
FEATURE [Part::Box] Box36025  label="Куб116"
  AttacherType = Attacher::AttachEngine3D
  Height = 65
  Length = 250
  Width = 120
FEATURE [Part::Compound] Compound_row3004
  Links = -> [Box36025,Box36002,Box36017,Box36011]
FEATURE [Part::Compound] Compound043  label="Труба"
  Links = -> [Compound_row3004,Compound_row3007,Compound_row3005,Compound_row3006,Compound_row3002,Compound_row3003]
  Placement = pos=(71,0,899) rot=(0,0,1;0rad)
FEATURE [Part::Compound] Compound038
  Links = -> [Box090,Box103,Box104,Box105,Box106]
  Placement = pos=(-1000,0,0) rot=(0,0,1;0rad)
FEATURE [Part::Box] Box133  label="Куб048"
  AttacherType = Attacher::AttachEngine3D
  Height = 120
  Length = 600
  Placement = pos=(-1000,251.73,456.377) rot=(1,0,0;0.785398rad)
  Width = 120
FEATURE [Part::Box] Box36026  label="Топка001"
  AttacherType = Attacher::AttachEngine3D
  Height = 255
  Length = 250
  Placement = pos=(128,-38,625) rot=(0,0,1;0rad)
  Width = 250
FEATURE [Part::Cut] Cut011
  Base = -> Compound042
  Tool = -> Box36026
FEATURE [Part::Box] Box101  label="Плита"
  AttacherType = Attacher::AttachEngine3D
  Height = 11
  Length = 410
  Placement = pos=(427,363,893) rot=(0,0,1;1.5708rad)
  Width = 340
